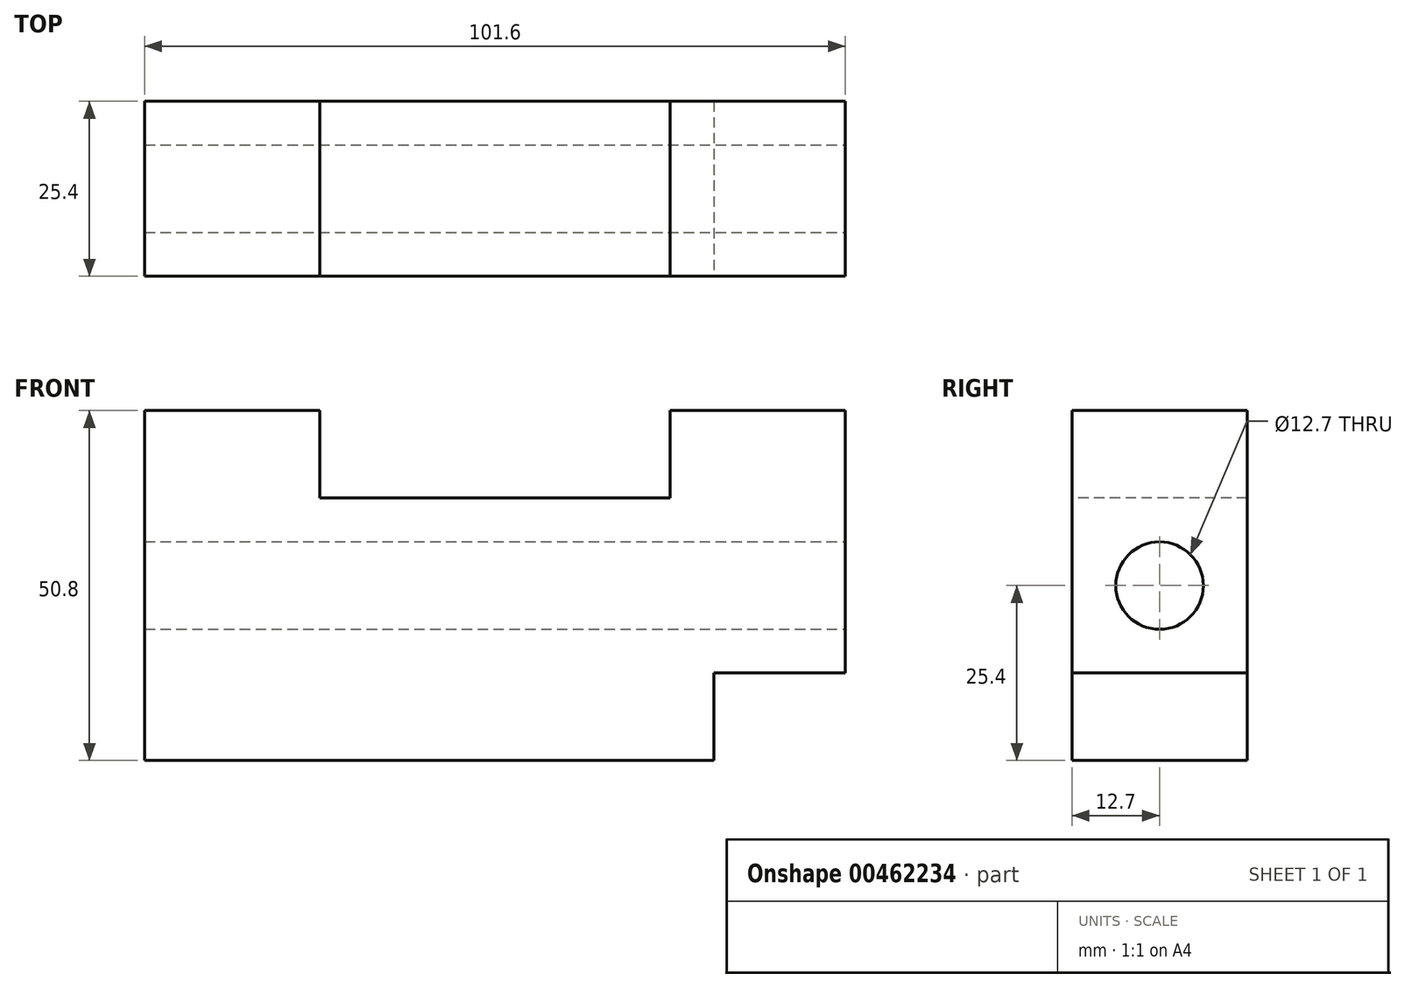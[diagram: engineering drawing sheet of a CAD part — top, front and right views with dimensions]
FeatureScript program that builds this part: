
annotation { "Feature Type Name" : "Feature", "Feature Type Description" : "" }
export const myFeature = defineFeature(function(context is Context, id is Id, definition is map)
    precondition{}
    {
        {
            var Q0;
            Q0=qCreatedBy(makeId("Front.planeOp"),FACE);
            var sketch = newSketch(context, id + "F0", { "sketchPlane" : qUnion([Q0])});
            skLineSegment(sketch, "E0.bottom", {"start": v(-50.8, -25.4) * mm, "end": v(50.8, -25.4) * mm});
            skLineSegment(sketch, "E0.top", {"start": v(-50.8, 25.4) * mm, "end": v(50.8, 25.4) * mm});
            skLineSegment(sketch, "E0.left", {"start": v(-50.8, -25.4) * mm, "end": v(-50.8, 25.4) * mm});
            skLineSegment(sketch, "E0.right", {"start": v(50.8, -25.4) * mm, "end": v(50.8, 25.4) * mm});
            skPoint(sketch, "E0.middle", {"position": v(0, 0) * mm});
            skLineSegment(sketch, "E1.bottom", {"start": v(50.8, -25.4) * mm, "end": v(31.75, -25.4) * mm});
            skLineSegment(sketch, "E1.top", {"start": v(50.8, -12.7) * mm, "end": v(31.75, -12.7) * mm});
            skLineSegment(sketch, "E1.left", {"start": v(50.8, -25.4) * mm, "end": v(50.8, -12.7) * mm});
            skLineSegment(sketch, "E1.right", {"start": v(31.75, -25.4) * mm, "end": v(31.75, -12.7) * mm});
            skSolve(sketch);
        }
        {
            var Q0;
            Q0 = qSketchRegion(id + "F0", true);
            extrude(context, id + "F1", {"entities" : qUnion([Q0]), "depth" : 25.4 * mm});
        }
        {
            var Q0;
            Q0=makeQuery(id+"F1.opExtrude","CAP_FACE",FACE,{"disambiguationData":[OSD([sQuery(id+"F0.wireOp",EDGE,"E0.bottom"),sQuery(id+"F0.wireOp",EDGE,"E0.top"),sQuery(id+"F0.wireOp",EDGE,"E0.left"),sQuery(id+"F0.wireOp",EDGE,"E0.right"),sQuery(id+"F0.wireOp",EDGE,"E1.bottom"),sQuery(id+"F0.wireOp",EDGE,"E1.left")])],"isStart":false});
            var sketch = newSketch(context, id + "F2", { "sketchPlane" : qUnion([Q0])});
            skLineSegment(sketch, "E2.bottom", {"start": v(50.8, -25.4) * mm, "end": v(31.75, -25.4) * mm});
            skLineSegment(sketch, "E2.top", {"start": v(50.8, -12.7) * mm, "end": v(31.75, -12.7) * mm});
            skLineSegment(sketch, "E2.left", {"start": v(50.8, -25.4) * mm, "end": v(50.8, -12.7) * mm});
            skLineSegment(sketch, "E2.right", {"start": v(31.75, -25.4) * mm, "end": v(31.75, -12.7) * mm});
            skSolve(sketch);
        }
        {
            var Q0;
            Q0 = qSketchRegion(id + "F2", true);
            extrude(context, id + "F3", {"entities" : qUnion([Q0]), "operationType" : NewBodyOperationType.REMOVE, "endBound" : BoundingType.THROUGH_ALL, "oppositeDirection" : true, "depth" : 25.4 * mm});
        }
        {
            var Q0;
            Q0=makeQuery(id+"F1.opExtrude","CAP_FACE",FACE,{"disambiguationData":[OSD([sQuery(id+"F0.wireOp",EDGE,"E0.bottom"),sQuery(id+"F0.wireOp",EDGE,"E0.top"),sQuery(id+"F0.wireOp",EDGE,"E0.left"),sQuery(id+"F0.wireOp",EDGE,"E0.right"),sQuery(id+"F0.wireOp",EDGE,"E1.bottom"),sQuery(id+"F0.wireOp",EDGE,"E1.left")])],"isStart":false});
            var sketch = newSketch(context, id + "F4", { "sketchPlane" : qUnion([Q0])});
            skLineSegment(sketch, "E3.bottom", {"start": v(-25.4, 25.4) * mm, "end": v(25.4, 25.4) * mm});
            skLineSegment(sketch, "E3.top", {"start": v(-25.4, 12.7) * mm, "end": v(25.4, 12.7) * mm});
            skLineSegment(sketch, "E3.left", {"start": v(-25.4, 25.4) * mm, "end": v(-25.4, 12.7) * mm});
            skLineSegment(sketch, "E3.right", {"start": v(25.4, 25.4) * mm, "end": v(25.4, 12.7) * mm});
            skSolve(sketch);
        }
        {
            var Q0;
            Q0 = qSketchRegion(id + "F4", true);
            extrude(context, id + "F5", {"entities" : qUnion([Q0]), "operationType" : NewBodyOperationType.REMOVE, "endBound" : BoundingType.THROUGH_ALL, "oppositeDirection" : true, "depth" : 25.4 * mm});
        }
        {
            var Q0;
            Q0=makeQuery(id+"F1.opExtrude","SWEPT_FACE",FACE,{"disambiguationData":[OSD([sQuery(id+"F0.wireOp",EDGE,"E0.right"),sQuery(id+"F0.wireOp",EDGE,"E1.left")])]});
            var sketch = newSketch(context, id + "F6", { "sketchPlane" : qUnion([Q0])});
            skCircle(sketch, "E4", {"center": v(-12.7, 0) * mm, "radius": 6.35 * mm});
            skSolve(sketch);
        }
        {
            var Q0;
            Q0 = qSketchRegion(id + "F6", true);
            extrude(context, id + "F7", {"entities" : qUnion([Q0]), "operationType" : NewBodyOperationType.REMOVE, "endBound" : BoundingType.THROUGH_ALL, "oppositeDirection" : true, "depth" : 25.4 * mm});
        }
    });
